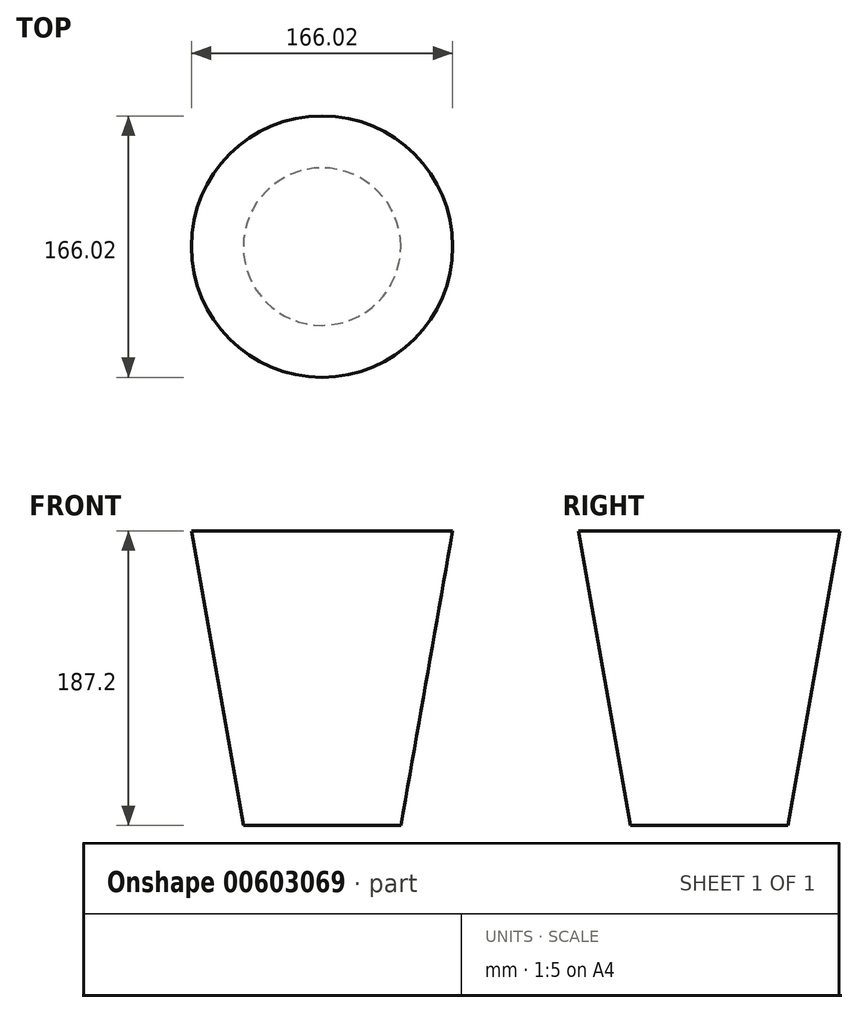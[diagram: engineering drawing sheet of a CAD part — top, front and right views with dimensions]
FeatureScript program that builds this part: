
annotation { "Feature Type Name" : "Feature", "Feature Type Description" : "" }
export const myFeature = defineFeature(function(context is Context, id is Id, definition is map)
    precondition{}
    {
        {
            var Q0;
            Q0=qCreatedBy(makeId("Top.planeOp"),FACE);
            var sketch = newSketch(context, id + "F0", { "sketchPlane" : qUnion([Q0])});
            skCircle(sketch, "E0", {"center": v(0, 0) * mm, "radius": 50 * mm});
            skSolve(sketch);
        }
        {
            var Q0;
            Q0=makeQuery(id+"F0.imprint","IMPRINT",FACE,{"disambiguationData":[TD([[makeQuery(id+"F0.imprint","IMPRINT",EDGE,{"derivedFrom":sQuery(id+"F0.wireOp",EDGE,"E0")}),1.0]])]});
            extrude(context, id + "F1", {"entities" : qUnion([Q0]), "depth" : 187.2 * mm, "offsetDistance" : 25 * mm, "hasDraft" : true, "draftAngle" : 10 * degree});
        }
    });
